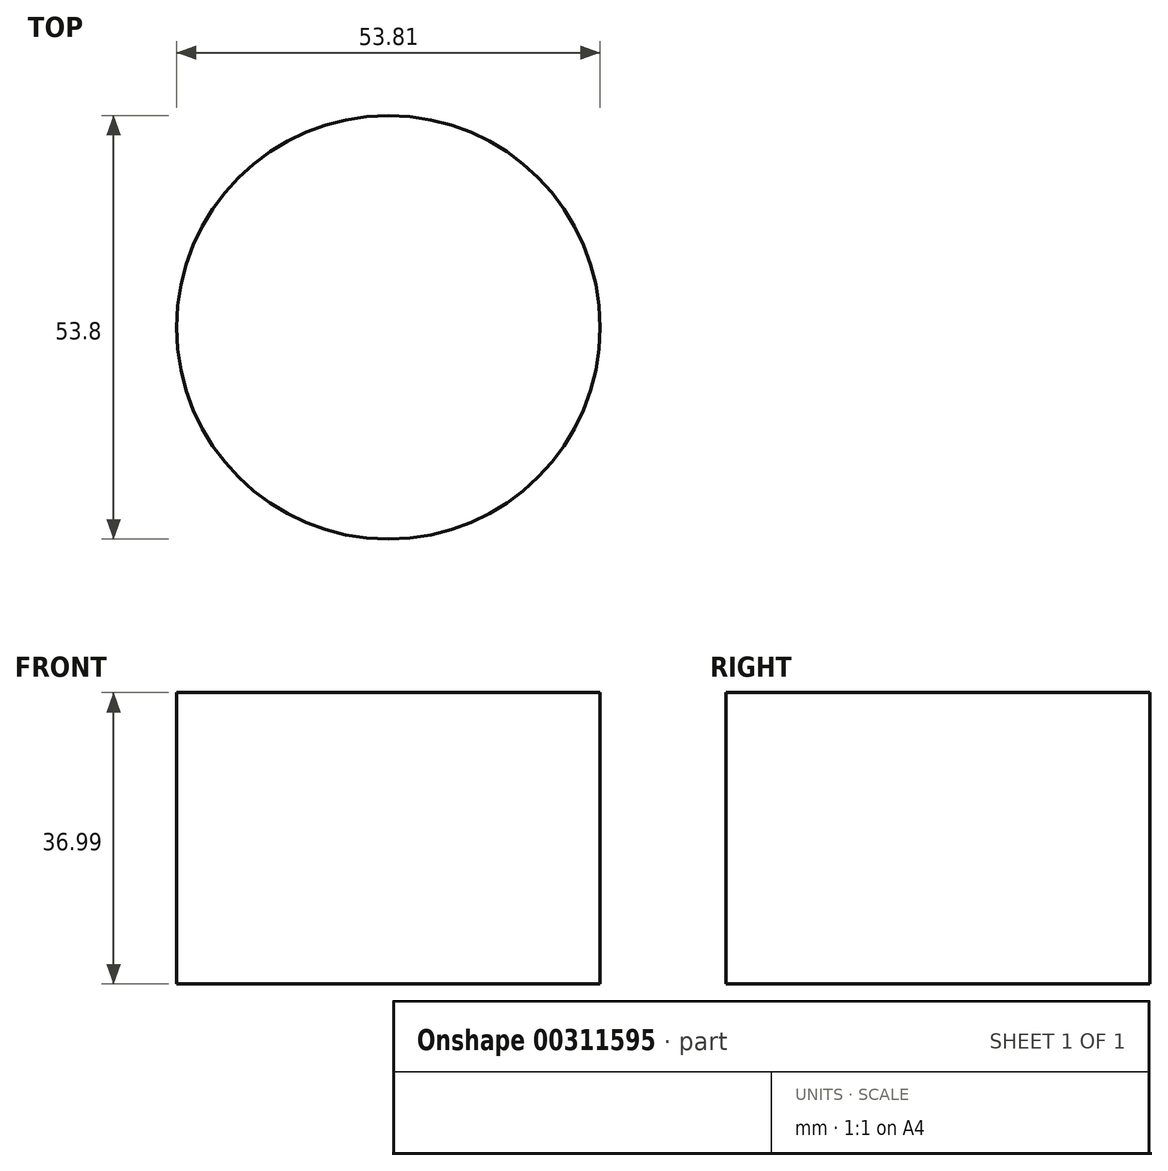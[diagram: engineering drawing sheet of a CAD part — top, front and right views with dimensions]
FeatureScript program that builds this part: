
annotation { "Feature Type Name" : "Feature", "Feature Type Description" : "" }
export const myFeature = defineFeature(function(context is Context, id is Id, definition is map)
    precondition{}
    {
        {
            var Q0;
            Q0=qCreatedBy(makeId("Front.planeOp"),FACE);
            var sketch = newSketch(context, id + "F0", { "sketchPlane" : qUnion([Q0])});
            skLineSegment(sketch, "E0.bottom", {"start": v(-10.93, 23.44) * mm, "end": v(-64.74, 23.44) * mm});
            skLineSegment(sketch, "E0.top", {"start": v(-10.93, 60.43) * mm, "end": v(-64.74, 60.43) * mm});
            skLineSegment(sketch, "E0.left", {"start": v(-10.93, 23.44) * mm, "end": v(-10.93, 60.43) * mm});
            skLineSegment(sketch, "E0.right", {"start": v(-64.74, 23.44) * mm, "end": v(-64.74, 60.43) * mm});
            skPoint(sketch, "E0.middle", {"position": v(-37.83, 41.93) * mm});
            skLineSegment(sketch, "E1", {"start": v(-37.83, 23.44) * mm, "end": v(-37.83, 60.43) * mm});
            skSolve(sketch);
        }
        {
            var Q0;
            {var subQ0=sQuery(id+"F0.wireOp",EDGE,"E0.left");Q0=makeQuery(id+"F0.imprint","IMPRINT",FACE,{"disambiguationData":[TD([[makeQuery(id+"F0.imprint","IMPRINT",EDGE,{"derivedFrom":subQ0}),1.0]])]});}
            var Q1;
            Q1=sQuery(id+"F0.wireOp",EDGE,"E1");
            revolve(context, id + "F1", {"entities" : qUnion([Q0]), "axis" : qUnion([Q1]), "revolveType" : RevolveType.FULL});
        }
    });
